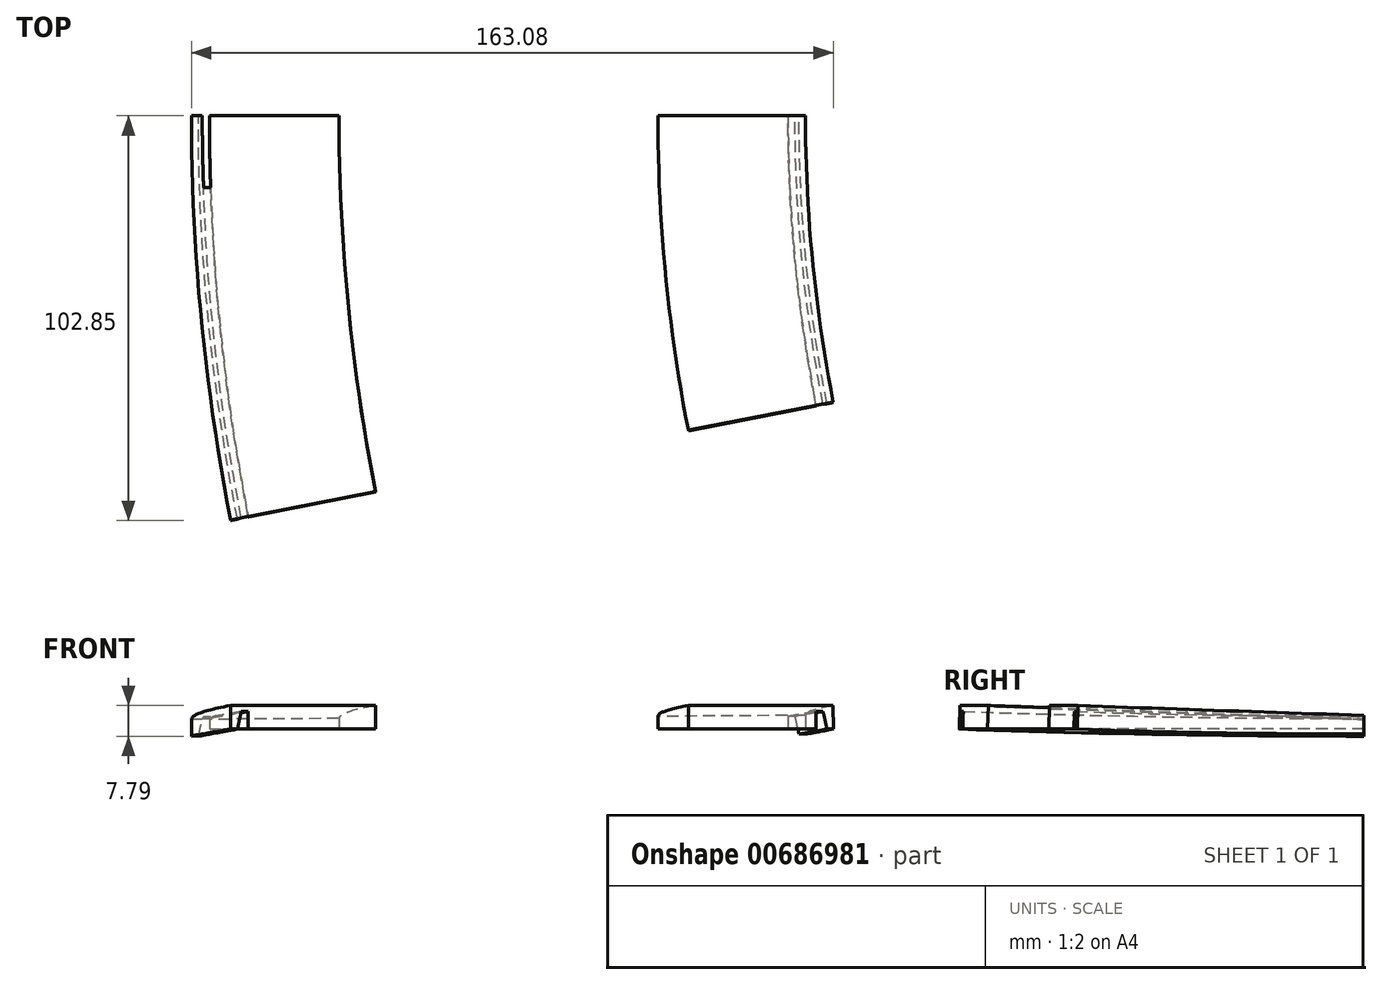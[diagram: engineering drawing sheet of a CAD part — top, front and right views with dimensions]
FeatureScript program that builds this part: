
annotation { "Feature Type Name" : "Feature", "Feature Type Description" : "" }
export const myFeature = defineFeature(function(context is Context, id is Id, definition is map)
    precondition{}
    {
        {
            var Q0;
            Q0=qCreatedBy(makeId("Front.planeOp"),FACE);
            var sketch = newSketch(context, id + "F0", { "sketchPlane" : qUnion([Q0])});
            skLineSegment(sketch, "E0", {"start": v(-0.07, -1.79) * mm, "end": v(534.04, 0) * mm});
            skLineSegment(sketch, "E1", {"start": v(534.04, 0) * mm, "end": v(517.63, 91.28) * mm});
            skLineSegment(sketch, "E2", {"start": v(517.63, 91.28) * mm, "end": v(-0.07, -1.79) * mm});
            skLineSegment(sketch, "E3", {"start": v(517.63, 91.28) * mm, "end": v(483.66, 280.23) * mm});
            skLineSegment(sketch, "E4", {"start": v(483.66, 280.23) * mm, "end": v(-34.04, 187.15) * mm});
            skArc(sketch, "E5", {"start": v(-34.04, 187.15) * mm, "mid": v(-22.42, 136.86) * mm, "end": v(-5.93, 87.94) * mm});
            skLineSegment(sketch, "E6", {"start": v(-5.93, 87.94) * mm, "end": v(483.66, 280.23) * mm});
            skLineSegment(sketch, "E7", {"start": v(-5.93, 87.94) * mm, "end": v(9.88, 0) * mm});
            skLineSegment(sketch, "E8", {"start": v(-0.07, -1.79) * mm, "end": v(0, -21.79) * mm});
            skLineSegment(sketch, "E9", {"start": v(0, -21.79) * mm, "end": v(156, -21.27) * mm});
            skLineSegment(sketch, "E10", {"start": v(156, -21.27) * mm, "end": v(155.93, -1.27) * mm});
            skLineSegment(sketch, "E11", {"start": v(118.43, -1.4) * mm, "end": v(118.5, -21.4) * mm});
            skLineSegment(sketch, "E12", {"start": v(37.43, -1.66) * mm, "end": v(37.5, -21.66) * mm});
            skSolve(sketch);
        }
        {
            var Q0;
            {var subQ0=sQuery(id+"F0.wireOp",EDGE,"E8");Q0=makeQuery(id+"F0.imprint","IMPRINT",FACE,{"disambiguationData":[TD([[makeQuery(id+"F0.imprint","IMPRINT",EDGE,{"derivedFrom":subQ0}),1.0]])]});}
            var Q1;
            {var subQ0=sQuery(id+"F0.wireOp",EDGE,"E10");Q1=makeQuery(id+"F0.imprint","IMPRINT",FACE,{"disambiguationData":[TD([[makeQuery(id+"F0.imprint","IMPRINT",EDGE,{"derivedFrom":subQ0}),1.0]])]});}
            var Q2;
            Q2=sQuery(id+"F0.wireOp",EDGE,"E1");
            revolve(context, id + "F1", {"entities" : qUnion([Q0, Q1]), "axis" : qUnion([Q2]), "revolveType" : RevolveType.SYMMETRIC, "angle" : 22.5 * degree});
        }
        {
            var Q0;
            Q0=qCreatedBy(makeId("Front.planeOp"),FACE);
            var sketch = newSketch(context, id + "F2", { "sketchPlane" : qUnion([Q0])});
            skLineSegment(sketch, "E13.bottom", {"start": v(4, -6.8) * mm, "end": v(152, -6.8) * mm});
            skLineSegment(sketch, "E13.top", {"start": v(4, -27.47) * mm, "end": v(152, -27.47) * mm});
            skLineSegment(sketch, "E13.left", {"start": v(4, -6.8) * mm, "end": v(4, -27.47) * mm});
            skLineSegment(sketch, "E13.right", {"start": v(152, -6.8) * mm, "end": v(152, -27.47) * mm});
            skLineSegment(sketch, "E14", {"start": v(526, 17.46) * mm, "end": v(526, -45.57) * mm});
            skSolve(sketch);
        }
        {
            var Q0;
            Q0=makeQuery(id+"F2.imprint","IMPRINT",FACE,{"disambiguationData":[TD([[makeQuery(id+"F2.imprint","IMPRINT",EDGE,{"derivedFrom":sQuery(id+"F2.wireOp",EDGE,"E13.bottom")}),-1.0]])]});
            var Q1;
            Q1=sQuery(id+"F2.wireOp",EDGE,"E14");
            revolve(context, id + "F3", {"operationType" : NewBodyOperationType.REMOVE, "entities" : qUnion([Q0]), "axis" : qUnion([Q1]), "revolveType" : RevolveType.ONE_DIRECTION, "oppositeDirection" : true, "angle" : 30 * degree});
        }
        {
            var Q0;
            Q0=makeQuery(id+"F1.opRevolve","CAP_FACE",FACE,{"disambiguationData":[OSD([sQuery(id+"F0.wireOp",EDGE,"E0"),sQuery(id+"F0.wireOp",EDGE,"E8"),sQuery(id+"F0.wireOp",EDGE,"E9"),sQuery(id+"F0.wireOp",EDGE,"E12")])],"isStart":false});
            var sketch = newSketch(context, id + "F4", { "sketchPlane" : qUnion([Q0])});
            skLineSegment(sketch, "E15", {"start": v(-21.02, -4.48) * mm, "end": v(69.55, -3.87) * mm});
            skLineSegment(sketch, "E16", {"start": v(69.55, -3.87) * mm, "end": v(67.88, 14.55) * mm});
            skLineSegment(sketch, "E17", {"start": v(67.88, 14.55) * mm, "end": v(-21.02, 9.42) * mm});
            skLineSegment(sketch, "E18", {"start": v(-21.02, 9.42) * mm, "end": v(-21.02, -4.48) * mm});
            skSolve(sketch);
        }
        {
            var Q0;
            {var subQ0=sQuery(id+"F4.wireOp",EDGE,"E16");Q0=makeQuery(id+"F4.imprint","IMPRINT",FACE,{"disambiguationData":[TD([[makeQuery(id+"F4.imprint","IMPRINT",EDGE,{"derivedFrom":subQ0}),1.0]])]});}
            var Q1;
            {var subQ4=sQuery(id+"F0.wireOp",EDGE,"E12");var subQ7=sQuery(id+"F0.wireOp",EDGE,"E0");var subQ8=makeQuery(id+"F1.opRevolve","CAP_EDGE",EDGE,{"disambiguationData":[OSD([subQ7]),TDD([makeQuery(id+"F0.imprint","IMPRINT",EDGE,{"disambiguationData":[TD([[makeQuery(id+"F0.imprint","INTERSECT",VERTEX,{"derivedFrom":[subQ7,subQ4]}),1.0]])],"derivedFrom":subQ7})])],"isStart":false});Q1=makeQuery(id+"F4.imprint","IMPRINT",FACE,{"disambiguationData":[TD([[makeQuery(id+"F4.imprint","IMPRINT",EDGE,{"derivedFrom":subQ8}),-1.0]])]});}
            extrude(context, id + "F5", {"entities" : qUnion([Q0, Q1]), "operationType" : NewBodyOperationType.REMOVE, "oppositeDirection" : true, "depth" : 236 * mm, "offsetDistance" : 25 * mm});
        }
        {
            var Q0;
            Q0=makeQuery(id+"F1.opRevolve","CAP_FACE",FACE,{"disambiguationData":[OSD([sQuery(id+"F0.wireOp",EDGE,"E0"),sQuery(id+"F0.wireOp",EDGE,"E9"),sQuery(id+"F0.wireOp",EDGE,"E10"),sQuery(id+"F0.wireOp",EDGE,"E11")])],"isStart":false});
            var sketch = newSketch(context, id + "F6", { "sketchPlane" : qUnion([Q0])});
            skLineSegment(sketch, "E19", {"start": v(98.4, -3.68) * mm, "end": v(187.2, -3.08) * mm});
            skLineSegment(sketch, "E20", {"start": v(187.2, -3.08) * mm, "end": v(179.32, 20.88) * mm});
            skLineSegment(sketch, "E21", {"start": v(179.32, 20.88) * mm, "end": v(100.36, 19.04) * mm});
            skLineSegment(sketch, "E22", {"start": v(100.36, 19.04) * mm, "end": v(98.4, -3.68) * mm});
            skSolve(sketch);
        }
        {
            var Q0;
            {var subQ0=sQuery(id+"F6.wireOp",EDGE,"E20");Q0=makeQuery(id+"F6.imprint","IMPRINT",FACE,{"disambiguationData":[TD([[makeQuery(id+"F6.imprint","IMPRINT",EDGE,{"derivedFrom":subQ0}),1.0]])]});}
            var Q1;
            {var subQ4=sQuery(id+"F0.wireOp",EDGE,"E10");var subQ7=sQuery(id+"F0.wireOp",EDGE,"E0");var subQ8=makeQuery(id+"F1.opRevolve","CAP_EDGE",EDGE,{"disambiguationData":[OSD([subQ7]),TDD([makeQuery(id+"F0.imprint","IMPRINT",EDGE,{"disambiguationData":[TD([[makeQuery(id+"F0.imprint","INTERSECT",VERTEX,{"derivedFrom":[subQ7,subQ4]}),1.0]])],"derivedFrom":subQ7})])],"isStart":false});Q1=makeQuery(id+"F6.imprint","IMPRINT",FACE,{"disambiguationData":[TD([[makeQuery(id+"F6.imprint","IMPRINT",EDGE,{"derivedFrom":subQ8}),-1.0]])]});}
            extrude(context, id + "F7", {"entities" : qUnion([Q0, Q1]), "operationType" : NewBodyOperationType.REMOVE, "oppositeDirection" : true, "depth" : 186.2 * mm, "offsetDistance" : 25 * mm});
        }
        {
            var Q0;
            Q0=qCreatedBy(makeId("Front.planeOp"),FACE);
            var sketch = newSketch(context, id + "F8", { "sketchPlane" : qUnion([Q0])});
            skLineSegment(sketch, "E23.bottom", {"start": v(197.8, 46.18) * mm, "end": v(-40.18, 46.18) * mm});
            skLineSegment(sketch, "E23.top", {"start": v(197.8, -65.27) * mm, "end": v(-40.18, -65.27) * mm});
            skLineSegment(sketch, "E23.left", {"start": v(197.8, 46.18) * mm, "end": v(197.8, -65.27) * mm});
            skLineSegment(sketch, "E23.right", {"start": v(-40.18, 46.18) * mm, "end": v(-40.18, -65.27) * mm});
            skSolve(sketch);
        }
        {
            var Q0;
            Q0=makeQuery(id+"F8.imprint","IMPRINT",FACE,{"disambiguationData":[TD([[makeQuery(id+"F8.imprint","IMPRINT",EDGE,{"derivedFrom":sQuery(id+"F8.wireOp",EDGE,"E23.bottom")}),1.0]])]});
            extrude(context, id + "F9", {"entities" : qUnion([Q0]), "operationType" : NewBodyOperationType.REMOVE, "oppositeDirection" : true, "depth" : 169 * mm, "offsetDistance" : 25 * mm});
        }
        {
            var Q0;
            Q0=qCreatedBy(makeId("Front.planeOp"),FACE);
            var sketch = newSketch(context, id + "F10", { "sketchPlane" : qUnion([Q0])});
            skLineSegment(sketch, "E24", {"start": v(0, -1.79) * mm, "end": v(534.11, 0) * mm});
            skLineSegment(sketch, "E25", {"start": v(534.11, 0) * mm, "end": v(517.7, 91.28) * mm});
            skLineSegment(sketch, "E26", {"start": v(517.7, 91.28) * mm, "end": v(0, -1.79) * mm});
            skLineSegment(sketch, "E27", {"start": v(517.7, 91.28) * mm, "end": v(487.6, 258.76) * mm});
            skLineSegment(sketch, "E28", {"start": v(487.6, 258.76) * mm, "end": v(-30.1, 165.7) * mm});
            skArc(sketch, "E29", {"start": v(-30.1, 165.7) * mm, "mid": v(-18.5, 115.4) * mm, "end": v(-2, 66.48) * mm});
            skLineSegment(sketch, "E30", {"start": v(-2, 66.48) * mm, "end": v(487.6, 258.76) * mm});
            skLineSegment(sketch, "E31", {"start": v(-2, 66.48) * mm, "end": v(9.95, 0) * mm});
            skLineSegment(sketch, "E32", {"start": v(0, -1.79) * mm, "end": v(0.07, -21.79) * mm});
            skLineSegment(sketch, "E33", {"start": v(0.07, -21.79) * mm, "end": v(156.07, -21.27) * mm});
            skLineSegment(sketch, "E34", {"start": v(156.07, -21.27) * mm, "end": v(156, -1.27) * mm});
            skLineSegment(sketch, "E35", {"start": v(0.02, -8.59) * mm, "end": v(1.72, -8.58) * mm});
            skLineSegment(sketch, "E36", {"start": v(1.72, -8.58) * mm, "end": v(2.72, -4.08) * mm});
            skLineSegment(sketch, "E37", {"start": v(2.72, -4.08) * mm, "end": v(4.52, -4.08) * mm});
            skLineSegment(sketch, "E38", {"start": v(4.52, -4.08) * mm, "end": v(4.58, -21.77) * mm});
            skLineSegment(sketch, "E39", {"start": v(156.02, -8.07) * mm, "end": v(154.32, -8.07) * mm});
            skLineSegment(sketch, "E40", {"start": v(154.32, -8.07) * mm, "end": v(153.32, -3.57) * mm});
            skLineSegment(sketch, "E41", {"start": v(153.32, -3.57) * mm, "end": v(151.52, -3.58) * mm});
            skLineSegment(sketch, "E42", {"start": v(151.52, -3.58) * mm, "end": v(151.58, -21.28) * mm});
            skLineSegment(sketch, "E43", {"start": v(0.02, -8.59) * mm, "end": v(-1.33, -7.73) * mm});
            skLineSegment(sketch, "E44", {"start": v(-1.33, -7.73) * mm, "end": v(-1.28, -22.97) * mm});
            skLineSegment(sketch, "E45", {"start": v(-1.28, -22.97) * mm, "end": v(0.07, -21.79) * mm});
            skSolve(sketch);
        }
        {
            var Q0;
            {var subQ0=sQuery(id+"F10.wireOp",EDGE,"E35");Q0=makeQuery(id+"F10.imprint","IMPRINT",FACE,{"disambiguationData":[TD([[makeQuery(id+"F10.imprint","IMPRINT",EDGE,{"derivedFrom":subQ0}),-1.0]])]});}
            var Q1;
            {var subQ0=sQuery(id+"F10.wireOp",EDGE,"E39");Q1=makeQuery(id+"F10.imprint","IMPRINT",FACE,{"disambiguationData":[TD([[makeQuery(id+"F10.imprint","IMPRINT",EDGE,{"derivedFrom":subQ0}),1.0]])]});}
            var Q2;
            {var subQ2=sQuery(id+"F10.wireOp",EDGE,"E43");Q2=makeQuery(id+"F10.imprint","IMPRINT",FACE,{"disambiguationData":[TD([[makeQuery(id+"F10.imprint","IMPRINT",EDGE,{"derivedFrom":subQ2}),1.0]])]});}
            var Q3;
            Q3=sQuery(id+"F10.wireOp",EDGE,"E25");
            revolve(context, id + "F11", {"operationType" : NewBodyOperationType.REMOVE, "entities" : qUnion([Q0, Q1, Q2]), "axis" : qUnion([Q3]), "revolveType" : RevolveType.ONE_DIRECTION, "angle" : 30 * degree});
        }
        {
            var Q0;
            Q0=qCreatedBy(makeId("Front.planeOp"),FACE);
            var sketch = newSketch(context, id + "F12", { "sketchPlane" : qUnion([Q0])});
            skLineSegment(sketch, "E46", {"start": v(0, -1.79) * mm, "end": v(534.11, 0) * mm});
            skLineSegment(sketch, "E47", {"start": v(534.11, 0) * mm, "end": v(517.7, 91.28) * mm});
            skLineSegment(sketch, "E48", {"start": v(517.7, 91.28) * mm, "end": v(0, -1.79) * mm});
            skLineSegment(sketch, "E49", {"start": v(517.7, 91.28) * mm, "end": v(489.6, 247.61) * mm});
            skLineSegment(sketch, "E50", {"start": v(489.6, 247.61) * mm, "end": v(-28.1, 154.54) * mm});
            skArc(sketch, "E51", {"start": v(-28.1, 154.54) * mm, "mid": v(-16.49, 104.25) * mm, "end": v(0, 55.33) * mm});
            skLineSegment(sketch, "E52", {"start": v(0, 55.33) * mm, "end": v(489.6, 247.61) * mm});
            skLineSegment(sketch, "E53", {"start": v(0, 55.33) * mm, "end": v(9.95, 0) * mm});
            skLineSegment(sketch, "E54", {"start": v(0, -1.79) * mm, "end": v(0.07, -21.79) * mm});
            skLineSegment(sketch, "E55", {"start": v(0.07, -21.79) * mm, "end": v(156.07, -21.27) * mm});
            skLineSegment(sketch, "E56", {"start": v(156.07, -21.27) * mm, "end": v(156, -1.27) * mm});
            skLineSegment(sketch, "E57", {"start": v(0.02, -8.59) * mm, "end": v(1.72, -8.58) * mm});
            skLineSegment(sketch, "E58", {"start": v(1.72, -8.58) * mm, "end": v(2.72, -4.08) * mm});
            skLineSegment(sketch, "E59", {"start": v(2.72, -4.08) * mm, "end": v(4.52, -4.08) * mm});
            skLineSegment(sketch, "E60", {"start": v(4.52, -4.08) * mm, "end": v(4.58, -21.77) * mm});
            skLineSegment(sketch, "E61", {"start": v(156.02, -8.07) * mm, "end": v(154.32, -8.07) * mm});
            skLineSegment(sketch, "E62", {"start": v(154.32, -8.07) * mm, "end": v(153.32, -3.57) * mm});
            skLineSegment(sketch, "E63", {"start": v(153.32, -3.57) * mm, "end": v(151.52, -3.58) * mm});
            skLineSegment(sketch, "E64", {"start": v(151.52, -3.58) * mm, "end": v(151.58, -21.28) * mm});
            skLineSegment(sketch, "E65", {"start": v(2.72, -4.08) * mm, "end": v(2.72, -2.81) * mm});
            skLineSegment(sketch, "E66", {"start": v(2.72, -2.81) * mm, "end": v(4.52, -2.8) * mm});
            skLineSegment(sketch, "E67", {"start": v(4.52, -2.8) * mm, "end": v(4.52, -4.08) * mm});
            skSolve(sketch);
        }
        {
            var Q0;
            Q0=makeQuery(id+"F12.imprint","IMPRINT",FACE,{"disambiguationData":[TD([[makeQuery(id+"F12.imprint","IMPRINT",EDGE,{"derivedFrom":sQuery(id+"F12.wireOp",EDGE,"E59")}),1.0]])]});
            var Q1;
            Q1=sQuery(id+"F12.wireOp",EDGE,"E47");
            revolve(context, id + "F13", {"operationType" : NewBodyOperationType.REMOVE, "entities" : qUnion([Q0]), "axis" : qUnion([Q1]), "revolveType" : RevolveType.ONE_DIRECTION, "angle" : 2 * degree});
        }
    });
